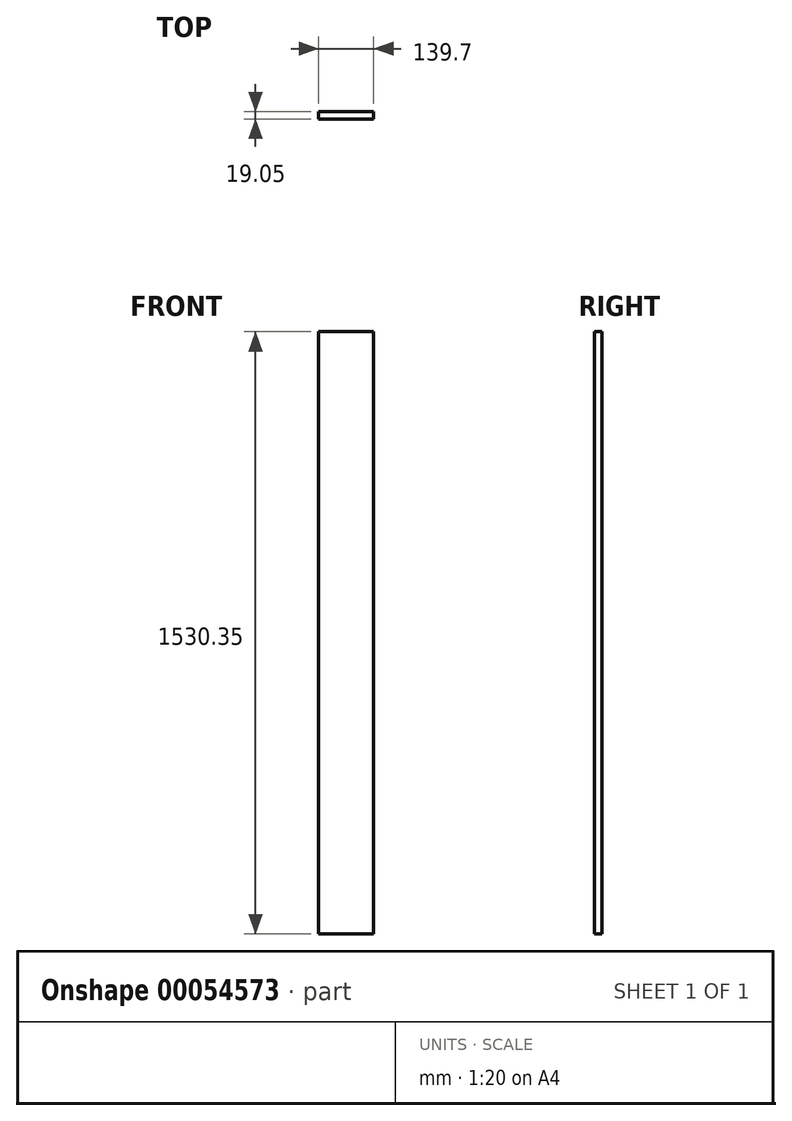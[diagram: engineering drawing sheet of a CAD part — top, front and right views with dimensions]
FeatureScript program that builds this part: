
annotation { "Feature Type Name" : "Feature", "Feature Type Description" : "" }
export const myFeature = defineFeature(function(context is Context, id is Id, definition is map)
    precondition{}
    {
        {
            var Q0;
            Q0=qCreatedBy(makeId("Top.planeOp"),FACE);
            var sketch = newSketch(context, id + "F0", { "sketchPlane" : qUnion([Q0])});
            skLineSegment(sketch, "E0.bottom", {"start": v(0, 0) * mm, "end": v(139.7, 0) * mm});
            skLineSegment(sketch, "E0.top", {"start": v(0, 19.05) * mm, "end": v(139.7, 19.05) * mm});
            skLineSegment(sketch, "E0.left", {"start": v(0, 0) * mm, "end": v(0, 19.05) * mm});
            skLineSegment(sketch, "E0.right", {"start": v(139.7, 0) * mm, "end": v(139.7, 19.05) * mm});
            skSolve(sketch);
        }
        {
            var Q0;
            Q0 = qSketchRegion(id + "F0", true);
            extrude(context, id + "F1", {"entities" : qUnion([Q0]), "depth" : 1530.35 * mm});
        }
    });
